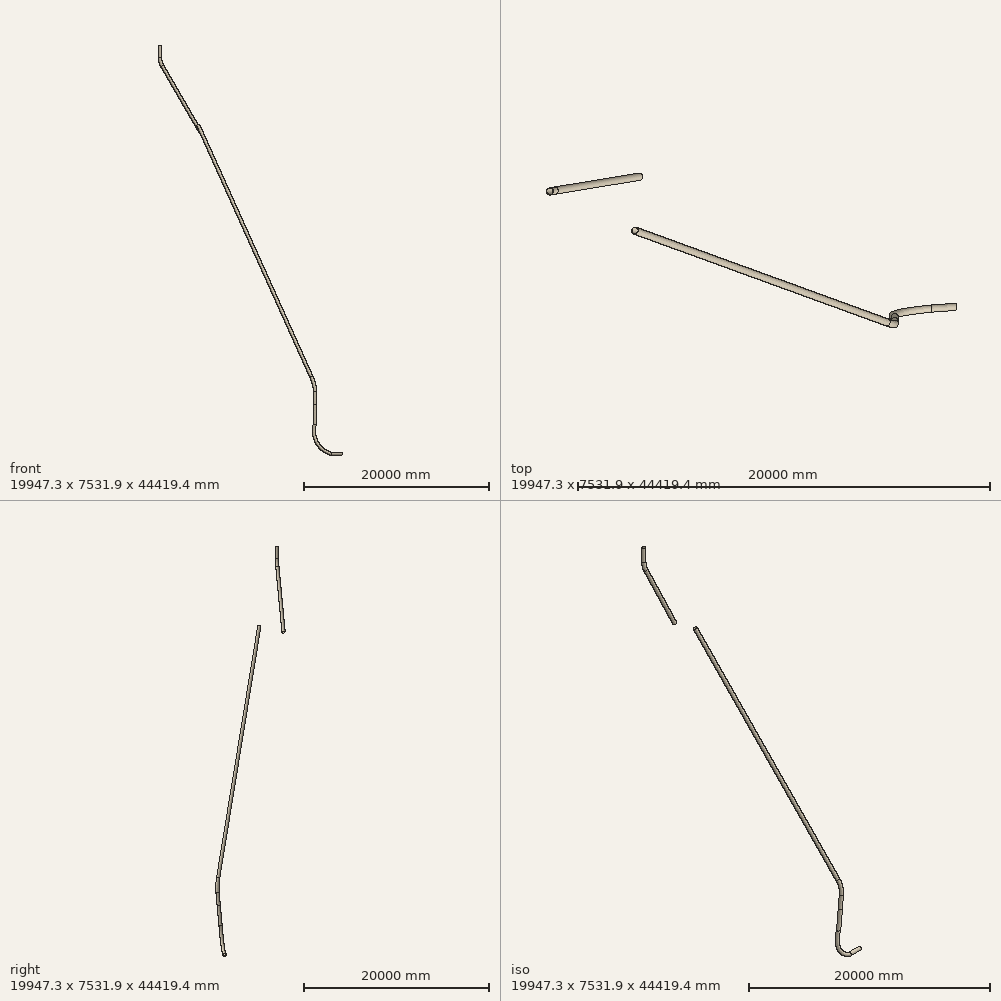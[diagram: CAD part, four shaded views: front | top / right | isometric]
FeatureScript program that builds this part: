
annotation { "Feature Type Name" : "Feature", "Feature Type Description" : "" }
export const myFeature = defineFeature(function(context is Context, id is Id, definition is map)
    precondition{}
    {
        {
            var Q0;
            Q0=qCreatedBy(makeId("Top.planeOp"),FACE);
            cPlane(context, id + "F0", {"entities" : qUnion([Q0]), "cplaneType" : CPlaneType.OFFSET, "offset" : 1812 * mm, "oppositeDirection" : true, "width" : 150 * mm, "height" : 150 * mm});
        }
        {
            var Q0;
            Q0=qCreatedBy(id+"F0.planeOp",FACE);
            cPlane(context, id + "F1", {"entities" : qUnion([Q0]), "cplaneType" : CPlaneType.OFFSET, "offset" : 7511 * mm, "oppositeDirection" : true, "width" : 150 * mm, "height" : 150 * mm});
        }
        {
            var Q0;
            Q0=qCreatedBy(id+"F1.planeOp",FACE);
            cPlane(context, id + "F2", {"entities" : qUnion([Q0]), "cplaneType" : CPlaneType.OFFSET, "offset" : 27110 * mm, "oppositeDirection" : true, "width" : 150 * mm, "height" : 150 * mm});
        }
        {
            var Q0;
            Q0=qCreatedBy(id+"F2.planeOp",FACE);
            cPlane(context, id + "F3", {"entities" : qUnion([Q0]), "cplaneType" : CPlaneType.OFFSET, "offset" : 6367 * mm, "oppositeDirection" : true, "width" : 150 * mm, "height" : 150 * mm});
        }
        {
            var Q0;
            Q0=qCreatedBy(makeId("Top.planeOp"),FACE);
            var sketch = newSketch(context, id + "F4", { "sketchPlane" : qUnion([Q0])});
            skLineSegment(sketch, "E0", {"start": v(0, 0) * mm, "end": v(0, 717) * mm, "construction": true});
            skLineSegment(sketch, "E1", {"start": v(0, 717) * mm, "end": v(4355, 717) * mm, "construction": true});
            skLineSegment(sketch, "E2", {"start": v(4355, 717) * mm, "end": v(0, 0) * mm, "construction": true});
            skSolve(sketch);
        }
        {
            var Q0;
            Q0=qCreatedBy(makeId("Front.planeOp"),FACE);
            var sketch = newSketch(context, id + "F5", { "sketchPlane" : qUnion([Q0])});
            skLineSegment(sketch, "E3", {"start": v(0, 0) * mm, "end": v(0, -1081.04) * mm, "construction": true});
            skSolve(sketch);
        }
        {
            var Q0;
            Q0=qCreatedBy(id+"F1.planeOp",FACE);
            var sketch = newSketch(context, id + "F6", { "sketchPlane" : qUnion([Q0])});
            skLineSegment(sketch, "E4", {"start": v(0, 0) * mm, "end": v(0, 717) * mm, "construction": true});
            skLineSegment(sketch, "E5", {"start": v(4355, 717) * mm, "end": v(0, 717) * mm, "construction": true});
            skSolve(sketch);
        }
        {
            var Q0;
            Q0=qCreatedBy(id+"F2.planeOp",FACE);
            var sketch = newSketch(context, id + "F7", { "sketchPlane" : qUnion([Q0])});
            skLineSegment(sketch, "E6", {"start": v(0, 0) * mm, "end": v(0, 717) * mm, "construction": true});
            skLineSegment(sketch, "E7", {"start": v(0, 717) * mm, "end": v(4355, 717) * mm, "construction": true});
            skLineSegment(sketch, "E8", {"start": v(4355, 717) * mm, "end": v(4355, -6310) * mm, "construction": true});
            skLineSegment(sketch, "E9", {"start": v(4355, -6310) * mm, "end": v(16779, -6310) * mm, "construction": true});
            skSolve(sketch);
        }
        {
            var Q0;
            Q0=sQuery(id+"F5.wireOp",VERTEX,"E3.end");
            var Q1;
            Q1=sQuery(id+"F5.wireOp",VERTEX,"E3.start");
            var Q2;
            Q2=sQuery(id+"F4.wireOp",VERTEX,"E2.start");
            cPlane(context, id + "F8", {"entities" : qUnion([Q0, Q1, Q2]), "cplaneType" : CPlaneType.THREE_POINT, "offset" : 25 * mm, "width" : 150 * mm, "height" : 150 * mm});
        }
        {
            var Q0;
            Q0=qCreatedBy(id+"F8.planeOp",FACE);
            var sketch = newSketch(context, id + "F9", { "sketchPlane" : qUnion([Q0])});
            skLineSegment(sketch, "E10", {"start": v(0, 0) * mm, "end": v(0, -1335.89) * mm});
            skLineSegment(sketch, "E11", {"start": v(241.21, -2222.49) * mm, "end": v(4413.63, -9323) * mm});
            skLineSegment(sketch, "E12", {"start": v(0, -1812) * mm, "end": v(0, -9323) * mm, "construction": true});
            skLineSegment(sketch, "E13", {"start": v(0, -9323) * mm, "end": v(4413.63, -9323) * mm, "construction": true});
            skPoint(sketch, "E14.visualSharp", {"position": v(0, -1812) * mm});
            skArc(sketch, "E14.filletArc", {"start": v(0, -1335.89) * mm, "mid": v(61.38, -1795.3) * mm, "end": v(241.21, -2222.49) * mm});
            skSolve(sketch);
        }
        {
            var Q0;
            Q0=sQuery(id+"F6.wireOp",VERTEX,"E5.end");
            var Q1;
            Q1=sQuery(id+"F7.wireOp",VERTEX,"E8.start");
            var Q2;
            Q2=sQuery(id+"F7.wireOp",VERTEX,"E9.end");
            cPlane(context, id + "F10", {"entities" : qUnion([Q0, Q1, Q2]), "cplaneType" : CPlaneType.THREE_POINT, "offset" : 25 * mm, "width" : 150 * mm, "height" : 150 * mm});
        }
        {
            var Q0;
            Q0=qCreatedBy(id+"F10.planeOp",FACE);
            var sketch = newSketch(context, id + "F11", { "sketchPlane" : qUnion([Q0])});
            skLineSegment(sketch, "E15", {"start": v(-3437.7, -9323) * mm, "end": v(-17509.74, -36050.26) * mm});
            skLineSegment(sketch, "E16", {"start": v(-17711.26, -36865.55) * mm, "end": v(-17711.26, -38933) * mm});
            skPoint(sketch, "E17.visualSharp", {"position": v(-17711.26, -36433) * mm});
            skArc(sketch, "E17.filletArc", {"start": v(-17509.74, -36050.26) * mm, "mid": v(-17660.13, -36445.64) * mm, "end": v(-17711.26, -36865.55) * mm});
            skSolve(sketch);
        }
        {
            var Q0;
            Q0=sQuery(id+"F11.wireOp",VERTEX,"E16.end");
            var Q1;
            Q1=sQuery(id+"F11.wireOp",VERTEX,"E17.visualSharp");
            var Q2;
            Q2=sQuery(id+"F7.wireOp",VERTEX,"E9.start");
            cPlane(context, id + "F12", {"entities" : qUnion([Q0, Q1, Q2]), "cplaneType" : CPlaneType.THREE_POINT, "offset" : 25 * mm, "width" : 150 * mm, "height" : 150 * mm});
        }
        {
            var Q0;
            Q0=qCreatedBy(id+"F12.planeOp",FACE);
            var sketch = newSketch(context, id + "F13", { "sketchPlane" : qUnion([Q0])});
            skLineSegment(sketch, "E18", {"start": v(-16779, -38933) * mm, "end": v(-16779, -41050) * mm});
            skLineSegment(sketch, "E19", {"start": v(-18529, -42800) * mm, "end": v(-19760, -42800) * mm});
            skPoint(sketch, "E20.visualSharp", {"position": v(-16779, -42800) * mm});
            skArc(sketch, "E20.filletArc", {"start": v(-18529, -42800) * mm, "mid": v(-17291.56, -42287.44) * mm, "end": v(-16779, -41050) * mm});
            skSolve(sketch);
        }
        {
            var Q0;
            Q0=qCreatedBy(id+"F2.planeOp",FACE);
            cPlane(context, id + "F14", {"entities" : qUnion([Q0]), "cplaneType" : CPlaneType.OFFSET, "offset" : 2500 * mm, "oppositeDirection" : true, "width" : 150 * mm, "height" : 150 * mm});
        }
        {
            var Q0;
            Q0=qCreatedBy(id+"F14.planeOp",FACE);
            var sketch = newSketch(context, id + "F15", { "sketchPlane" : qUnion([Q0])});
            skCircle(sketch, "E21", {"center": v(16779, -6310) * mm, "radius": 177.8 * mm});
            skCircle(sketch, "E22", {"center": v(16779, -6310) * mm, "radius": 158.7 * mm});
            skSolve(sketch);
        }
        {
            var Q0;
            Q0 = qSketchRegion(id + "F15", true);
            var Q1;
            Q1 = qConstructionFilter(qBodyType(qCreatedBy(id + "F13" ,EDGE), BodyType.WIRE), ConstructionObject.NO);
            sweep(context, id + "F16", {"profiles" : qUnion([Q0]), "path" : qUnion([Q1])});
        }
        {
            var Q0;
            Q0 = qSketchRegion(id + "F15", true);
            var Q1;
            Q1 = qConstructionFilter(qBodyType(qCreatedBy(id + "F11" ,EDGE), BodyType.WIRE), ConstructionObject.NO);
            sweep(context, id + "F17", {"operationType" : NewBodyOperationType.ADD, "profiles" : qUnion([Q0]), "path" : qUnion([Q1])});
        }
        {
            var Q0;
            Q0=qCreatedBy(makeId("Top.planeOp"),FACE);
            var sketch = newSketch(context, id + "F18", { "sketchPlane" : qUnion([Q0])});
            skCircle(sketch, "E23", {"center": v(0, 0) * mm, "radius": 177.8 * mm});
            skCircle(sketch, "E24", {"center": v(0, 0) * mm, "radius": 158.7 * mm});
            skSolve(sketch);
        }
        {
            var Q0;
            Q0 = qSketchRegion(id + "F18", true);
            var Q1;
            Q1 = qConstructionFilter(qBodyType(qCreatedBy(id + "F9" ,EDGE), BodyType.WIRE), ConstructionObject.NO);
            sweep(context, id + "F19", {"operationType" : NewBodyOperationType.ADD, "profiles" : qUnion([Q0]), "path" : qUnion([Q1])});
        }
    });
